# Revit family: Mixer_Sink_Nero_Bianca_PullOut_VegieSpray
name_source: partatom
category: Plumbing Fixtures
units: mm (PartAtom-declared; Revit-internal decimal feet)

## family parameters
Always vertical = Yes
Cut with Voids When Loaded = Yes
Maintain Annotation Orientation = No
OmniClass Number = 23.31.00.00
OmniClass Title = Plumbing Specific Products and Equipment
Part Type = Normal
Room Calculation Point = No
Round Connector Dimension = Use Diameter
Shared = No
Work Plane-Based = No

## types (6) — shared parameters
Assembly Code = D2010
CW Connection = Yes
Default Elevation = 900 mm
HW Connection = Yes
IfcExportAs = IfcValveType
IfcExportType = FAUCET
Manufacturer = Nero
ManufacturerOverallDepth = 261 mm
ManufacturerOverallHeight = 451.1 mm
ManufacturerOverallWidth = 111.5 mm
ManufacturerURLProductSpecific = https://nerotapware.com.au
ModifiedIssue = 20251105 $
URL = https://nerotapware.com.au
Uniclass2015Code = Pr_40_20_87
Uniclass2015Title = Taps and water supply outlet fittings
Uniclass2015Version = Products v1.35
Vent Connection = No
Waste Connection = No
zero-valued in all types: CWFU, HWFU, WFU

## per-type parameters (varying)
| type | Description | ManufacturerSpecCode | Material | Model | Type Comments |
| Chrome (NR321508CH) | Bianca Pull Out Sink Mixer With Vegie Spray Function Chrome | NR321508CH | Metal_Chrome_Nero | NR321508CH | Mixer - Sink - Pull Out - Vegie Spray - Chrome |
| Matte Black (NR321508MB) | Bianca Pull Out Sink Mixer With Vegie Spray Function Matte Black | NR321508MB | Metal_MatteBlack_Nero | NR321508MB | Mixer - Sink - Pull Out - Vegie Spray - Matte Black |
| Brushed Nickel (NR321508BN) | Bianca Pull Out Sink Mixer With Vegie Spray Function Brushed Nickel | NR321508BN | Metal_Nickel_Nero_Brushed | NR321508BN | Mixer - Sink - Pull Out - Vegie Spray - Brushed Nickel |
| Gunmetal (NR321508GM) | Bianca Pull Out Sink Mixer With Vegie Spray Function Gun Metal | NR321508GM | Metal_GunMetal_Nero | NR321508GM | Mixer - Sink - Pull Out - Vegie Spray - Gunmetal |
| Brushed Gold (NR321508BG) | Bianca Pull Out Sink Mixer With Vegie Spray Function Brushed Gold | NR321508BG | Metal_Gold_Nero_Brushed | NR321508BG | Mixer - Sink - Pull Out - Vegie Spray - Brushed Gold |
| Brushed Bronze (NR321508BZ) | Bianca Pull Out Sink Mixer With Vegie Spray Function Brushed Bronze | NR321508BZ | Metal_Bronze_Nero_Brushed | NR321508BZ | Mixer - Sink - Pull Out - Vegie Spray - Brushed Bronze |

## geometry (parser evidence)
native form markers: Sweep x2
no freeform markers — native parametric forms only
